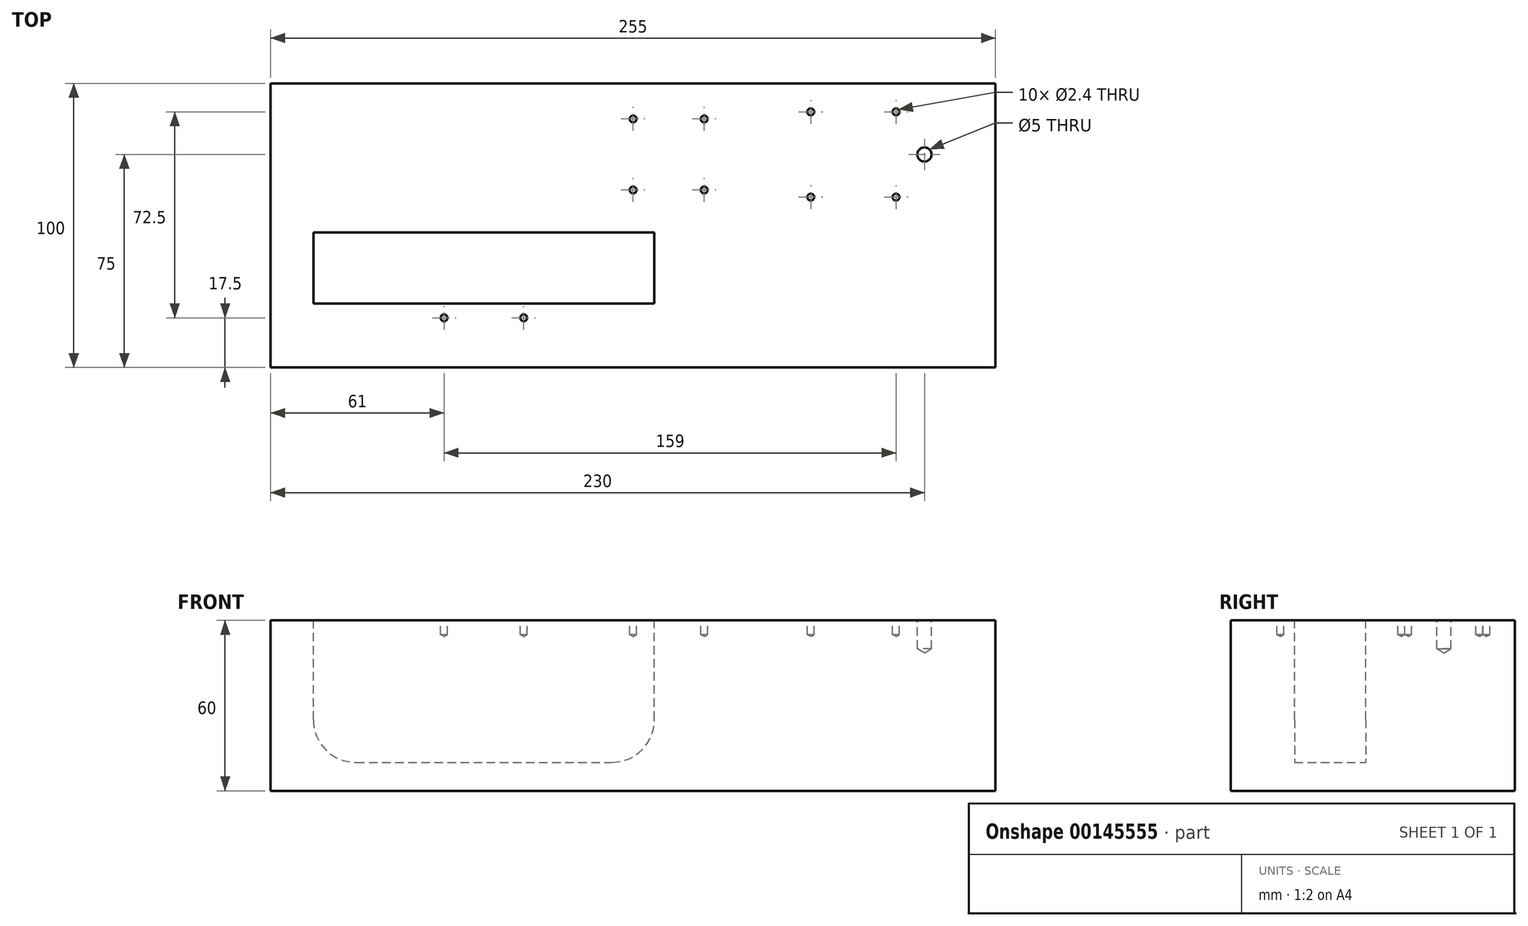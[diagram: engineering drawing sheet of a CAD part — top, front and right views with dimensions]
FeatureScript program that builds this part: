
annotation { "Feature Type Name" : "Feature", "Feature Type Description" : "" }
export const myFeature = defineFeature(function(context is Context, id is Id, definition is map)
    precondition{}
    {
        {
            var Q0;
            Q0=qCreatedBy(makeId("Top.planeOp"),FACE);
            var sketch = newSketch(context, id + "F0", { "sketchPlane" : qUnion([Q0])});
            skLineSegment(sketch, "E0.rect.bottom", {"start": v(127.5, 50) * mm, "end": v(-127.5, 50) * mm});
            skLineSegment(sketch, "E0.rect.top", {"start": v(127.5, -50) * mm, "end": v(-127.5, -50) * mm});
            skLineSegment(sketch, "E0.rect.left", {"start": v(127.5, 50) * mm, "end": v(127.5, -50) * mm});
            skLineSegment(sketch, "E0.rect.right", {"start": v(-127.5, 50) * mm, "end": v(-127.5, -50) * mm});
            skPoint(sketch, "E0.rect.middle", {"position": v(0, 0) * mm});
            skSolve(sketch);
        }
        {
            var Q0;
            Q0=qSketchRegion(id+"F0",true);
            extrude(context, id + "F1", {"entities" : qUnion([Q0]), "depth" : 60 * mm});
        }
        {
            var Q0;
            Q0=makeQuery(id+"F1.opExtrude","CAP_FACE",FACE,{"disambiguationData":[OSD([sQuery(id+"F0.wireOp",EDGE,"E0.rect.bottom"),sQuery(id+"F0.wireOp",EDGE,"E0.rect.top"),sQuery(id+"F0.wireOp",EDGE,"E0.rect.left"),sQuery(id+"F0.wireOp",EDGE,"E0.rect.right")])],"isStart":false});
            var sketch = newSketch(context, id + "F2", { "sketchPlane" : qUnion([Q0])});
            skLineSegment(sketch, "E1.bottom", {"start": v(-112.5, -27.5) * mm, "end": v(7.5, -27.5) * mm});
            skLineSegment(sketch, "E1.top", {"start": v(-112.5, -2.5) * mm, "end": v(7.5, -2.5) * mm});
            skLineSegment(sketch, "E1.left", {"start": v(-112.5, -27.5) * mm, "end": v(-112.5, -2.5) * mm});
            skLineSegment(sketch, "E1.right", {"start": v(7.5, -27.5) * mm, "end": v(7.5, -2.5) * mm});
            skLineSegment(sketch, "E2", {"start": v(-112.5, -15) * mm, "end": v(-73.47, -15) * mm, "construction": true});
            skLineSegment(sketch, "E3", {"start": v(-52.5, -27.5) * mm, "end": v(-52.5, -12.67) * mm, "construction": true});
            skSolve(sketch);
        }
        {
            var Q0;
            Q0=qSketchRegion(id+"F2",true);
            extrude(context, id + "F3", {"entities" : qUnion([Q0]), "operationType" : NewBodyOperationType.REMOVE, "oppositeDirection" : true, "depth" : 50 * mm});
        }
        {
            var Q0;
            Q0=makeQuery(id+"F3.boolean.opBoolean","COPY",EDGE,{"derivedFrom":makeQuery(id+"F3.opExtrude","CAP_EDGE",EDGE,{"disambiguationData":[OSD([sQuery(id+"F2.wireOp",EDGE,"E1.right")])],"isStart":false})});
            var Q1;
            Q1=makeQuery(id+"F3.boolean.opBoolean","COPY",EDGE,{"derivedFrom":makeQuery(id+"F3.opExtrude","CAP_EDGE",EDGE,{"disambiguationData":[OSD([sQuery(id+"F2.wireOp",EDGE,"E1.left")])],"isStart":false})});
            fillet(context, id + "F4", {"entities" : qUnion([Q0, Q1]), "radius" : 15 * mm, "tangentPropagation" : true, "allowEdgeOverflow" : false});
        }
        {
            var Q0;
            Q0=makeQuery(id+"F1.opExtrude","CAP_FACE",FACE,{"disambiguationData":[OSD([sQuery(id+"F0.wireOp",EDGE,"E0.rect.bottom"),sQuery(id+"F0.wireOp",EDGE,"E0.rect.top"),sQuery(id+"F0.wireOp",EDGE,"E0.rect.left"),sQuery(id+"F0.wireOp",EDGE,"E0.rect.right")])],"isStart":false});
            var sketch = newSketch(context, id + "F5", { "sketchPlane" : qUnion([Q0])});
            skLineSegment(sketch, "E4", {"start": v(49.86, 25) * mm, "end": v(77.5, 25) * mm, "construction": true});
            skLineSegment(sketch, "E5", {"start": v(62.5, 40) * mm, "end": v(62.5, 10) * mm, "construction": true});
            skLineSegment(sketch, "E6", {"start": v(92.5, 10) * mm, "end": v(92.5, 40) * mm, "construction": true});
            skLineSegment(sketch, "E7", {"start": v(49.86, 25) * mm, "end": v(12.5, 25) * mm, "construction": true});
            skLineSegment(sketch, "E8.rect.bottom", {"start": v(0, 12.5) * mm, "end": v(25, 12.5) * mm, "construction": true});
            skLineSegment(sketch, "E8.rect.top", {"start": v(0, 37.5) * mm, "end": v(25, 37.5) * mm, "construction": true});
            skLineSegment(sketch, "E8.rect.left", {"start": v(0, 12.5) * mm, "end": v(0, 37.5) * mm, "construction": true});
            skLineSegment(sketch, "E8.rect.right", {"start": v(25, 12.5) * mm, "end": v(25, 37.5) * mm, "construction": true});
            skPoint(sketch, "E8.rect.middle", {"position": v(12.5, 25) * mm});
            skLineSegment(sketch, "E9", {"start": v(77.5, 25) * mm, "end": v(77.5, 12.47) * mm, "construction": true});
            skPoint(sketch, "E10", {"position": v(25, 25) * mm});
            skLineSegment(sketch, "E11", {"start": v(12.5, 25) * mm, "end": v(-52.5, 25) * mm, "construction": true});
            skLineSegment(sketch, "E12", {"start": v(-52.5, 25) * mm, "end": v(-52.5, -45.45) * mm, "construction": true});
            skLineSegment(sketch, "E13", {"start": v(-66.5, -32.5) * mm, "end": v(-38.5, -32.5) * mm, "construction": true});
            skLineSegment(sketch, "E14", {"start": v(77.5, 25) * mm, "end": v(102.5, 25) * mm, "construction": true});
            skSolve(sketch);
        }
        {
            var Q0;
            Q0=sQuery(id+"F5.wireOp",VERTEX,"E6.start");
            var Q1;
            Q1=sQuery(id+"F5.wireOp",VERTEX,"E6.end");
            var Q2;
            Q2=sQuery(id+"F5.wireOp",VERTEX,"E5.end");
            var Q3;
            Q3=sQuery(id+"F5.wireOp",VERTEX,"E5.start");
            var Q4;
            Q4=sQuery(id+"F5.wireOp",VERTEX,"E8.rect.right.start");
            var Q5;
            Q5=sQuery(id+"F5.wireOp",VERTEX,"E8.rect.left.start");
            var Q6;
            Q6=sQuery(id+"F5.wireOp",VERTEX,"E8.rect.left.end");
            var Q7;
            Q7=sQuery(id+"F5.wireOp",VERTEX,"E8.rect.right.end");
            var Q8;
            Q8=sQuery(id+"F5.wireOp",VERTEX,"E13.end");
            var Q9;
            Q9=sQuery(id+"F5.wireOp",VERTEX,"E13.start");
            var Q10;
            Q10=makeQuery(id+"F1.opExtrude","SWEPT_BODY",BODY,{"disambiguationData":[OSD([sQuery(id+"F0.wireOp",EDGE,"E0.rect.bottom"),sQuery(id+"F0.wireOp",EDGE,"E0.rect.top"),sQuery(id+"F0.wireOp",EDGE,"E0.rect.left"),sQuery(id+"F0.wireOp",EDGE,"E0.rect.right")])]});
            hole(context, id + "F6", {"style" : HoleStyle.SIMPLE, "holeDiameter" : 2.4 * mm, "endStyle" : HoleEndStyle.BLIND, "holeDepth" : 5 * mm, "locations" : qUnion([Q0, Q1, Q2, Q3, Q4, Q5, Q6, Q7, Q8, Q9]), "scope" : qUnion([Q10])});
        }
        {
            var Q0;
            Q0=sQuery(id+"F5.wireOp",VERTEX,"E14.end");
            var Q1;
            Q1=makeQuery(id+"F1.opExtrude","SWEPT_BODY",BODY,{"disambiguationData":[OSD([sQuery(id+"F0.wireOp",EDGE,"E0.rect.bottom"),sQuery(id+"F0.wireOp",EDGE,"E0.rect.top"),sQuery(id+"F0.wireOp",EDGE,"E0.rect.left"),sQuery(id+"F0.wireOp",EDGE,"E0.rect.right")])]});
            hole(context, id + "F7", {"style" : HoleStyle.SIMPLE, "holeDiameter" : 5 * mm, "endStyle" : HoleEndStyle.BLIND, "holeDepth" : 10 * mm, "locations" : qUnion([Q0]), "scope" : qUnion([Q1])});
        }
    });
